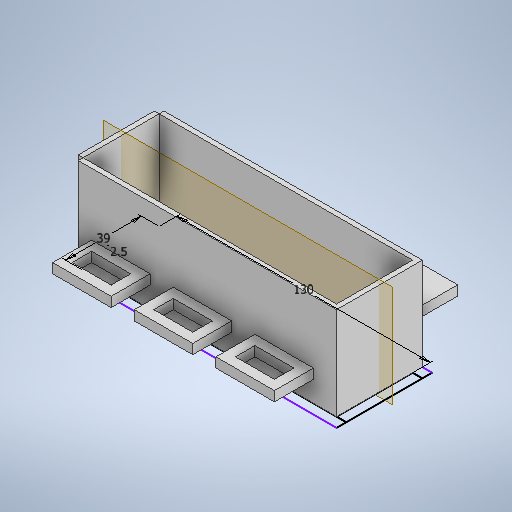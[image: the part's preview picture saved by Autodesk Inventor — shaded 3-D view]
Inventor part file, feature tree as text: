
AUTODESK INVENTOR PART (.ipt)
format: ipt  version: 2025 (Build 290162010, 162A)  size: 391,680 bytes
history: native  units: in
note: dims shown in document units (in); Inventor stores cm internally (conversion verified against a paired STEP export)
features: move_body x8, sketch x7, direct_edit x6, extrude x5, plane x1, mirror x1
ambient origin geometry x8: Origin, YZ Plane, XZ Plane, XY Plane, X Axis, Y Axis, Z Axis, Center Point
bodies: Solid1 (feature_tree)
feature tree (28):
  sketch  "Sketch1"  dims[d0=5.1181in d1=1.5354in]
  extrude  "Extrusion1"  Depth=1.5354in
  sketch  "Sketch2"  dims[d2=0.1969in d3=0.0in d4=1.7717in d5=0.0in]
  sketch  "Sketch3"  dims[d6=0.0in d7=0.0in d8=-0.0984in d9=0.0in d10=0.0in d11=-0.0984in]
  sketch  "Sketch4"  dims[d12=0.0in d13=0.0in d14=-0.0984in d15=0.0in d16=0.0in d17=-0.0984in]
  sketch  "Sketch5"  dims[d18=1.1811in d19=0.1969in]
  extrude  "Extrusion2"  Depth=1.7717in TaperAngle=0.0deg
  direct_edit  "Direct Edit1"
  direct_edit  "Direct Edit2"
  sketch  "Sketch6"  dims[d20=0.4183in]
  direct_edit  "Direct Edit3"
  direct_edit  "Direct Edit4"
  extrude  "Extrusion3"  TaperAngle=0.0deg  [1 undecoded]
  direct_edit  "Direct Edit5"
  extrude  "Extrusion4"  TaperAngle=0.0deg  [1 undecoded]
  extrude  "Extrusion5"  Depth=0.1969in
  direct_edit  "Direct Edit6"
  plane  "Work Plane1"
  mirror  "Mirror1"
  sketch  "Sketch7"  dims[d21=0.0in d22=0.0in d23=-0.1969in d24=0.0in d25=0.0in d26=0.1969in d27=1.6732in d28=1.1811in d29=0.1969in d30=1.1811in d31=0.1969in d32=0.4675in d33=0.4675in d34=0.4675in d35=5.4134in d36=0.4675in d37=1.1811in d38=0.0in d39=0.0in d40=0.0in d41=-0.3937in d42=0.1969in d43=0.7874in d44=0.3937in d45=1.1811in d46=0.7874in d47=0.1969in d48=1.6486in d49=0.7874in d50=0.3937in d51=0.7874in d52=0.3937in d53=1.1811in d54=0.0in d55=0.0984in d56=1.1811in d57=0.0in d58=0.0in d59=0.0in d60=-0.0984in]
  move_body  "Move1"
  move_body  "Move2"
  move_body  "Move3"
  move_body  "Move4"
  move_body  "Move5"
  move_body  "Move6"
  move_body  "Move7"
  move_body  "Move8"
note: 2 required parameter values undecoded (feature->parameter linkage not recoverable at this tier; creation-order binding heuristic only, values carry confidence <= 0.55)
